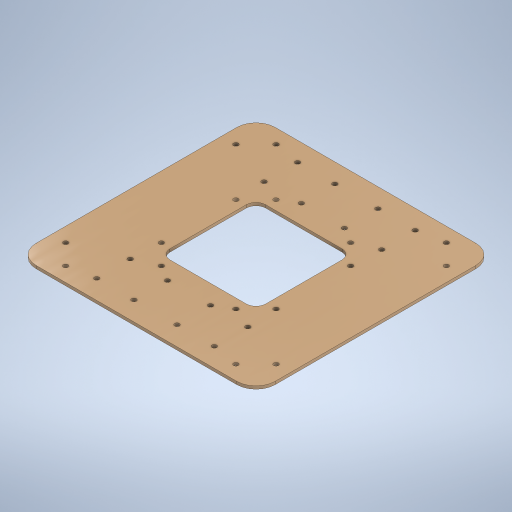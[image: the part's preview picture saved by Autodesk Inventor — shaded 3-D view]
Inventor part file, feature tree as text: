
AUTODESK INVENTOR PART (.ipt)
format: ipt  version: 2024 (Build 280153000, 153)  size: 368,128 bytes
history: native  units: in
note: dims shown in document units (in); Inventor stores cm internally (conversion verified against a paired STEP export)
features: sketch x3, hole x2, other x1, extrude x1
ambient origin geometry x8: Origin, YZ Plane, XZ Plane, XY Plane, X Axis, Y Axis, Z Axis, Center Point
bodies: Body1 (feature_tree)
feature tree (7):
  other  "Main Body"
  extrude  "Main Body Extrusion"  Depth=0.3937in
  hole  "Bracket Holes"  [1 undecoded]
  hole  "Hole4"  [1 undecoded]
  sketch  "Sketch3"  dims[d86=9.8425in d87=9.8425in d88=0.1969in d89=0.2953in d90=0.1476in d91=0.0984in d92=90.0deg d93=0.3937in d94=0.8108in d95=1.1811in]
  sketch  "Sketch11"  dims[d96=1.1811in d97=0.7874in]
  sketch  "Sketch12"  dims[d98=0.7874in d99=0.3937in d100=0.3937in d101=0.1575in d102=0.1969in d103=0.1969in d104=0.1575in d105=1.5748in d107=360.0deg d109=0.1969in d110=0.2953in d111=0.1476in d112=0.0984in d113=90.0deg d114=0.3937in d115=0.8108in d116=1.1811in d117=1.1811in d118=0.7874in d119=0.7874in d120=0.1575in d121=0.1969in d122=0.1969in d123=0.1575in d124=2.3622in d125=2.3622in d126=0.7874in d127=3.937in d128=3.937in d129=0.3937in d130=1.5748in d132=360.0deg d38=0.0394in d39=0.0394in d40=0.0394in d41=0.0059in d42=0.0098in d43=0.0148in d44=32.2835in d45=0.0295in d46=46.4567in d47=0.0025in d48=0.0295in d49=0.0148in d65=0.1969in d66=1.9685in d67=0.1969in d68=1.9685in]
note: 2 required parameter values undecoded (feature->parameter linkage not recoverable at this tier; creation-order binding heuristic only, values carry confidence <= 0.55)
